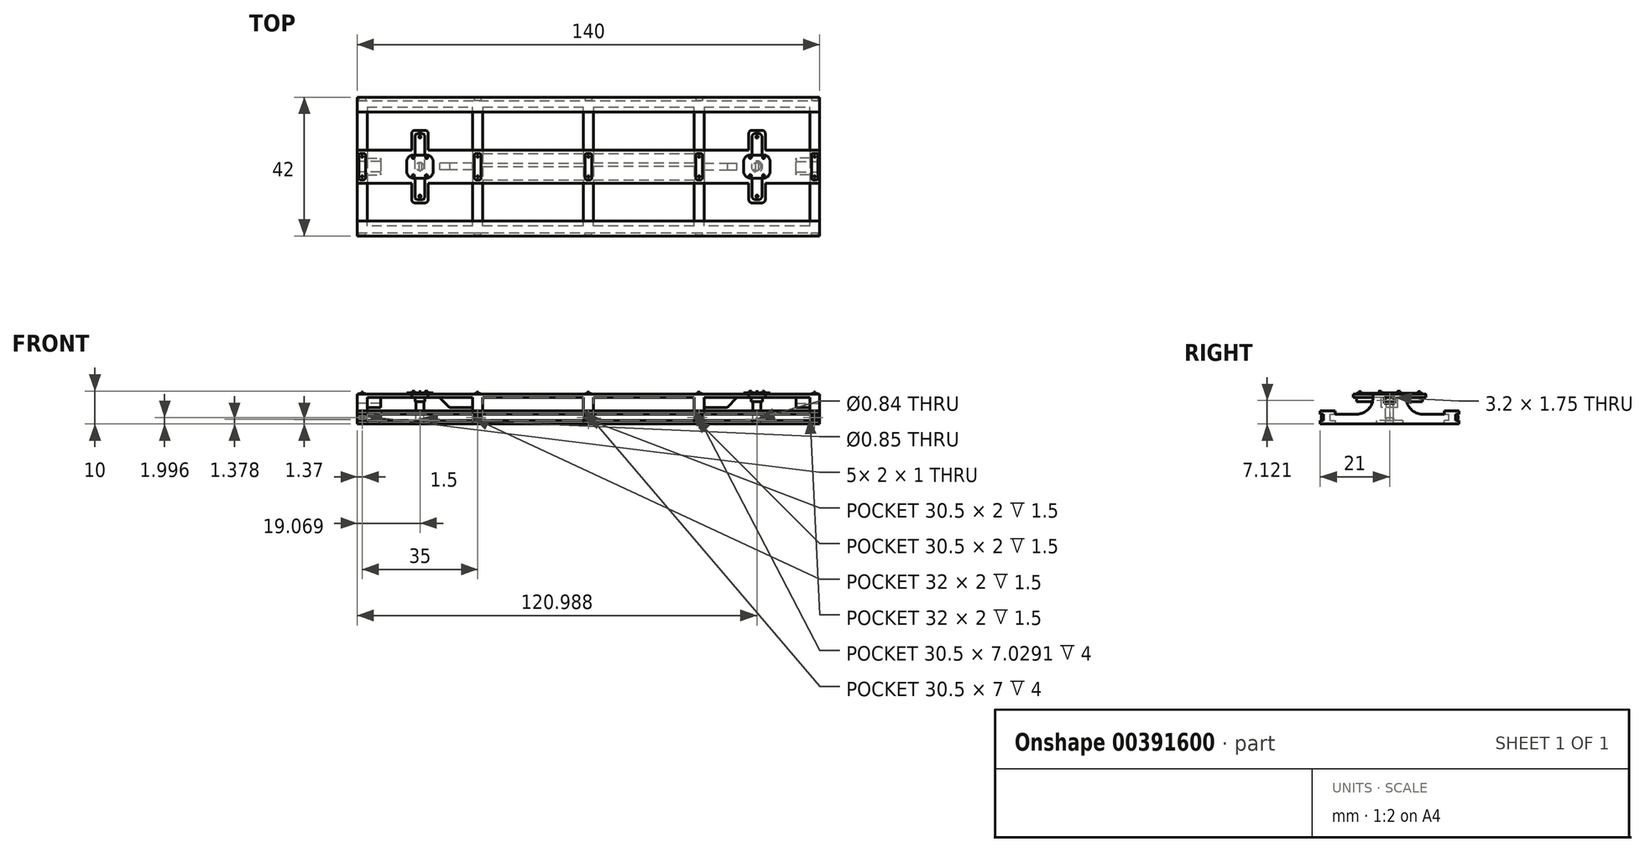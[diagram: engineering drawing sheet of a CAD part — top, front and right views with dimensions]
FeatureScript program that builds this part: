
annotation { "Feature Type Name" : "Feature", "Feature Type Description" : "" }
export const myFeature = defineFeature(function(context is Context, id is Id, definition is map)
    precondition{}
    {
        {
            var Q0;
            Q0=qCreatedBy(makeId("Right.planeOp"),FACE);
            var sketch = newSketch(context, id + "F0", { "sketchPlane" : qUnion([Q0])});
            skLineSegment(sketch, "E0", {"start": v(-20, 2.38) * mm, "end": v(-20, -0.62) * mm});
            skLineSegment(sketch, "E1", {"start": v(-20, -0.62) * mm, "end": v(20, -0.62) * mm});
            skLineSegment(sketch, "E2", {"start": v(20, -0.62) * mm, "end": v(20, 2.38) * mm});
            skLineSegment(sketch, "E3", {"start": v(20, 2.38) * mm, "end": v(10, 2.38) * mm});
            skLineSegment(sketch, "E4", {"start": v(5, 7.38) * mm, "end": v(5, 8.38) * mm});
            skLineSegment(sketch, "E5", {"start": v(5, 8.38) * mm, "end": v(-5, 8.38) * mm});
            skLineSegment(sketch, "E6", {"start": v(-5, 8.38) * mm, "end": v(-5, 7.38) * mm});
            skLineSegment(sketch, "E7", {"start": v(-10, 2.38) * mm, "end": v(-20, 2.38) * mm});
            skPoint(sketch, "E8.visualSharp", {"position": v(-5, 2.38) * mm});
            skArc(sketch, "E8.filletArc", {"start": v(-10, 2.38) * mm, "mid": v(-6.46, 3.84) * mm, "end": v(-5, 7.38) * mm});
            skPoint(sketch, "E9.visualSharp", {"position": v(5, 2.38) * mm});
            skArc(sketch, "E9.filletArc", {"start": v(5, 7.38) * mm, "mid": v(6.46, 3.84) * mm, "end": v(10, 2.38) * mm});
            skSolve(sketch);
        }
        {
            var Q0;
            Q0=makeQuery(id+"F0.imprint","IMPRINT",FACE,{"disambiguationData":[TD([[makeQuery(id+"F0.imprint","IMPRINT",EDGE,{"derivedFrom":sQuery(id+"F0.wireOp",EDGE,"E0")}),1.0]])]});
            extrude(context, id + "F1", {"entities" : qUnion([Q0]), "endBound" : BoundingType.SYMMETRIC, "depth" : 140 * mm});
        }
        {
            var Q0;
            Q0=makeQuery(id+"F1.opExtrude","SWEPT_FACE",FACE,{"disambiguationData":[OSD([sQuery(id+"F0.wireOp",EDGE,"E0")])]});
            var sketch = newSketch(context, id + "F2", { "sketchPlane" : qUnion([Q0])});
            skLineSegment(sketch, "E10.bottom", {"start": v(-67, 7.38) * mm, "end": v(-35, 7.38) * mm});
            skLineSegment(sketch, "E10.top", {"start": v(-67, -0.62) * mm, "end": v(-35, -0.62) * mm});
            skLineSegment(sketch, "E10.left", {"start": v(-67, 7.38) * mm, "end": v(-67, -0.62) * mm});
            skLineSegment(sketch, "E10.right", {"start": v(-35, 7.38) * mm, "end": v(-35, -0.62) * mm});
            skLineSegment(sketch, "E11.bottom", {"start": v(35, 7.38) * mm, "end": v(67, 7.38) * mm});
            skLineSegment(sketch, "E11.top", {"start": v(35, -0.62) * mm, "end": v(67, -0.62) * mm});
            skLineSegment(sketch, "E11.left", {"start": v(35, 7.38) * mm, "end": v(35, -0.62) * mm});
            skLineSegment(sketch, "E11.right", {"start": v(67, 7.38) * mm, "end": v(67, -0.62) * mm});
            skSolve(sketch);
        }
        {
            var Q0;
            Q0 = qSketchRegion(id + "F2", true);
            extrude(context, id + "F3", {"entities" : qUnion([Q0]), "operationType" : NewBodyOperationType.REMOVE, "endBound" : BoundingType.THROUGH_ALL, "oppositeDirection" : true, "depth" : 25 * mm});
        }
        {
            var Q0;
            Q0=makeQuery(id+"F3.boolean.opBoolean","SPLIT",FACE,{"disambiguationData":[TD([makeQuery(id+"F3.opExtrude","SWEPT_FACE",FACE,{"disambiguationData":[OSD([sQuery(id+"F2.wireOp",EDGE,"E10.right")])]})])],"derivedFrom":makeQuery(id+"F1.opExtrude","SWEPT_FACE",FACE,{"disambiguationData":[OSD([sQuery(id+"F0.wireOp",EDGE,"E0")])]})});
            var sketch = newSketch(context, id + "F4", { "sketchPlane" : qUnion([Q0])});
            skLineSegment(sketch, "E12.bottom", {"start": v(-32, 7.38) * mm, "end": v(-1.5, 7.38) * mm});
            skLineSegment(sketch, "E12.top", {"start": v(-32, -0.62) * mm, "end": v(-1.5, -0.62) * mm});
            skLineSegment(sketch, "E12.left", {"start": v(-32, 7.38) * mm, "end": v(-32, -0.62) * mm});
            skLineSegment(sketch, "E12.right", {"start": v(-1.5, 7.38) * mm, "end": v(-1.5, -0.62) * mm});
            skLineSegment(sketch, "E13.bottom", {"start": v(32, 7.4) * mm, "end": v(1.5, 7.4) * mm});
            skLineSegment(sketch, "E13.top", {"start": v(32, -0.62) * mm, "end": v(1.5, -0.62) * mm});
            skLineSegment(sketch, "E13.left", {"start": v(32, 7.4) * mm, "end": v(32, -0.62) * mm});
            skLineSegment(sketch, "E13.right", {"start": v(1.5, 7.4) * mm, "end": v(1.5, -0.62) * mm});
            skSolve(sketch);
        }
        {
            var Q0;
            Q0 = qSketchRegion(id + "F4", true);
            extrude(context, id + "F5", {"entities" : qUnion([Q0]), "operationType" : NewBodyOperationType.REMOVE, "endBound" : BoundingType.THROUGH_ALL, "oppositeDirection" : true, "depth" : 25 * mm});
        }
        {
            var Q0;
            Q0=makeQuery(id+"F1.opExtrude","CAP_FACE",FACE,{"disambiguationData":[OSD([sQuery(id+"F0.wireOp",EDGE,"E0"),sQuery(id+"F0.wireOp",EDGE,"E1"),sQuery(id+"F0.wireOp",EDGE,"E2"),sQuery(id+"F0.wireOp",EDGE,"E3"),sQuery(id+"F0.wireOp",EDGE,"E4"),sQuery(id+"F0.wireOp",EDGE,"E5"),sQuery(id+"F0.wireOp",EDGE,"E6"),sQuery(id+"F0.wireOp",EDGE,"E7"),sQuery(id+"F0.wireOp",EDGE,"E8.filletArc"),sQuery(id+"F0.wireOp",EDGE,"E9.filletArc")])],"isStart":false});
            var sketch = newSketch(context, id + "F6", { "sketchPlane" : qUnion([Q0])});
            skLineSegment(sketch, "E14.bottom", {"start": v(-20, 2.38) * mm, "end": v(-18, 2.38) * mm});
            skLineSegment(sketch, "E14.top", {"start": v(-20, -0.62) * mm, "end": v(-18, -0.62) * mm});
            skLineSegment(sketch, "E14.left", {"start": v(-20, 2.38) * mm, "end": v(-20, -0.62) * mm});
            skLineSegment(sketch, "E14.right", {"start": v(-18, 2.38) * mm, "end": v(-18, -0.62) * mm});
            skLineSegment(sketch, "E15.bottom", {"start": v(20, 2.38) * mm, "end": v(18, 2.38) * mm});
            skLineSegment(sketch, "E15.top", {"start": v(20, -0.62) * mm, "end": v(18, -0.62) * mm});
            skLineSegment(sketch, "E15.left", {"start": v(20, 2.38) * mm, "end": v(20, -0.62) * mm});
            skLineSegment(sketch, "E15.right", {"start": v(18, 2.38) * mm, "end": v(18, -0.62) * mm});
            skSolve(sketch);
        }
        {
            var Q0;
            Q0 = qSketchRegion(id + "F6", true);
            extrude(context, id + "F7", {"entities" : qUnion([Q0]), "operationType" : NewBodyOperationType.ADD, "oppositeDirection" : true, "depth" : 140 * mm});
        }
        {
            var Q0;
            Q0=makeQuery(id+"F1.opExtrude","CAP_FACE",FACE,{"disambiguationData":[OSD([sQuery(id+"F0.wireOp",EDGE,"E0"),sQuery(id+"F0.wireOp",EDGE,"E1"),sQuery(id+"F0.wireOp",EDGE,"E2"),sQuery(id+"F0.wireOp",EDGE,"E3"),sQuery(id+"F0.wireOp",EDGE,"E4"),sQuery(id+"F0.wireOp",EDGE,"E5"),sQuery(id+"F0.wireOp",EDGE,"E6"),sQuery(id+"F0.wireOp",EDGE,"E7"),sQuery(id+"F0.wireOp",EDGE,"E8.filletArc"),sQuery(id+"F0.wireOp",EDGE,"E9.filletArc")])],"isStart":false});
            var sketch = newSketch(context, id + "F8", { "sketchPlane" : qUnion([Q0])});
            skLineSegment(sketch, "E16.bottom", {"start": v(-21, 3.38) * mm, "end": v(-16.5, 3.38) * mm});
            skLineSegment(sketch, "E16.top", {"start": v(-21, 2.38) * mm, "end": v(-16.5, 2.38) * mm});
            skLineSegment(sketch, "E16.left", {"start": v(-21, 3.38) * mm, "end": v(-21, 2.38) * mm});
            skLineSegment(sketch, "E16.right", {"start": v(-16.5, 3.38) * mm, "end": v(-16.5, 2.38) * mm});
            skLineSegment(sketch, "E17.bottom", {"start": v(16.5, 2.38) * mm, "end": v(21, 2.38) * mm});
            skLineSegment(sketch, "E17.top", {"start": v(16.5, 3.38) * mm, "end": v(21, 3.38) * mm});
            skLineSegment(sketch, "E17.left", {"start": v(16.5, 2.38) * mm, "end": v(16.5, 3.38) * mm});
            skLineSegment(sketch, "E17.right", {"start": v(21, 2.38) * mm, "end": v(21, 3.38) * mm});
            skSolve(sketch);
        }
        {
            var Q0;
            Q0 = qSketchRegion(id + "F8", true);
            extrude(context, id + "F9", {"entities" : qUnion([Q0]), "operationType" : NewBodyOperationType.ADD, "oppositeDirection" : true, "depth" : 140 * mm});
        }
        {
            var Q0;
            Q0=makeQuery(id+"F9.boolean.opBoolean","MERGE",FACE,{"derivedFrom":[makeQuery(id+"F1.opExtrude","CAP_FACE",FACE,{"disambiguationData":[OSD([sQuery(id+"F0.wireOp",EDGE,"E0"),sQuery(id+"F0.wireOp",EDGE,"E1"),sQuery(id+"F0.wireOp",EDGE,"E2"),sQuery(id+"F0.wireOp",EDGE,"E3"),sQuery(id+"F0.wireOp",EDGE,"E4"),sQuery(id+"F0.wireOp",EDGE,"E5"),sQuery(id+"F0.wireOp",EDGE,"E6"),sQuery(id+"F0.wireOp",EDGE,"E7"),sQuery(id+"F0.wireOp",EDGE,"E8.filletArc"),sQuery(id+"F0.wireOp",EDGE,"E9.filletArc")])],"isStart":false}),makeQuery(id+"F9.opExtrude","CAP_FACE",FACE,{"disambiguationData":[OSD([sQuery(id+"F8.wireOp",EDGE,"E16.bottom"),sQuery(id+"F8.wireOp",EDGE,"E16.top"),sQuery(id+"F8.wireOp",EDGE,"E16.left"),sQuery(id+"F8.wireOp",EDGE,"E16.right")])],"isStart":true}),makeQuery(id+"F9.opExtrude","CAP_FACE",FACE,{"disambiguationData":[OSD([sQuery(id+"F8.wireOp",EDGE,"E17.bottom"),sQuery(id+"F8.wireOp",EDGE,"E17.top"),sQuery(id+"F8.wireOp",EDGE,"E17.left"),sQuery(id+"F8.wireOp",EDGE,"E17.right")])],"isStart":true})]});
            var sketch = newSketch(context, id + "F10", { "sketchPlane" : qUnion([Q0])});
            skLineSegment(sketch, "E18.bottom", {"start": v(-16.5, -0.62) * mm, "end": v(-21, -0.62) * mm});
            skLineSegment(sketch, "E18.top", {"start": v(-16.5, 0.38) * mm, "end": v(-21, 0.38) * mm});
            skLineSegment(sketch, "E18.left", {"start": v(-16.5, -0.62) * mm, "end": v(-16.5, 0.38) * mm});
            skLineSegment(sketch, "E18.right", {"start": v(-21, -0.62) * mm, "end": v(-21, 0.38) * mm});
            skLineSegment(sketch, "E19.bottom", {"start": v(16.5, 0.38) * mm, "end": v(21, 0.38) * mm});
            skLineSegment(sketch, "E19.top", {"start": v(16.5, -0.62) * mm, "end": v(21, -0.62) * mm});
            skLineSegment(sketch, "E19.left", {"start": v(16.5, 0.38) * mm, "end": v(16.5, -0.62) * mm});
            skLineSegment(sketch, "E19.right", {"start": v(21, 0.38) * mm, "end": v(21, -0.62) * mm});
            skSolve(sketch);
        }
        {
            var Q0;
            Q0 = qSketchRegion(id + "F10", true);
            extrude(context, id + "F11", {"entities" : qUnion([Q0]), "operationType" : NewBodyOperationType.ADD, "oppositeDirection" : true, "depth" : 140 * mm});
        }
        {
            var Q0;
            Q0=makeQuery(id+"F3.boolean.opBoolean","COPY",FACE,{"derivedFrom":makeQuery(id+"F3.opExtrude","SWEPT_FACE",FACE,{"disambiguationData":[OSD([sQuery(id+"F2.wireOp",EDGE,"E11.bottom")])]})});
            var sketch = newSketch(context, id + "F12", { "sketchPlane" : qUnion([Q0])});
            skCircle(sketch, "E20", {"center": v(51, 0) * mm, "radius": 1.2 * mm});
            skCircle(sketch, "E21", {"center": v(-51, 0) * mm, "radius": 1.2 * mm});
            skSolve(sketch);
        }
        {
            var Q0;
            Q0 = qSketchRegion(id + "F12", true);
            extrude(context, id + "F13", {"entities" : qUnion([Q0]), "operationType" : NewBodyOperationType.ADD, "depth" : 8 * mm});
        }
        {
            var Q0;
            Q0=makeQuery(id+"F3.boolean.opBoolean","COPY",FACE,{"derivedFrom":makeQuery(id+"F3.opExtrude","SWEPT_FACE",FACE,{"disambiguationData":[OSD([sQuery(id+"F2.wireOp",EDGE,"E10.bottom")])]})});
            var sketch = newSketch(context, id + "F14", { "sketchPlane" : qUnion([Q0])});
            skLineSegment(sketch, "E22.bottom", {"start": v(-52.5, 10) * mm, "end": v(-49.5, 10) * mm});
            skLineSegment(sketch, "E22.top", {"start": v(-52.5, -10) * mm, "end": v(-49.5, -10) * mm});
            skLineSegment(sketch, "E22.left", {"start": v(-52.5, 10) * mm, "end": v(-52.5, -10) * mm});
            skLineSegment(sketch, "E22.right", {"start": v(-49.5, 10) * mm, "end": v(-49.5, -10) * mm});
            skCircle(sketch, "E23", {"center": v(51.03, 0) * mm, "radius": 1.7 * mm});
            skSolve(sketch);
        }
        {
            var Q0;
            Q0 = qSketchRegion(id + "F14", true);
            extrude(context, id + "F15", {"entities" : qUnion([Q0]), "operationType" : NewBodyOperationType.ADD, "depth" : 1.2 * mm});
        }
        {
            var Q0;
            Q0=makeQuery(id+"F1.opExtrude","SWEPT_FACE",FACE,{"disambiguationData":[OSD([sQuery(id+"F0.wireOp",EDGE,"E5")])]});
            var sketch = newSketch(context, id + "F16", { "sketchPlane" : qUnion([Q0])});
            skLineSegment(sketch, "E24.bottom", {"start": v(-53, 3.5) * mm, "end": v(-49, 3.5) * mm});
            skLineSegment(sketch, "E24.top", {"start": v(-53, -3.5) * mm, "end": v(-49, -3.5) * mm});
            skLineSegment(sketch, "E24.left", {"start": v(-55, 1.5) * mm, "end": v(-55, -1.5) * mm});
            skLineSegment(sketch, "E24.right", {"start": v(-47, 1.5) * mm, "end": v(-47, -1.5) * mm});
            skLineSegment(sketch, "E25.bottom", {"start": v(49, 3.5) * mm, "end": v(53, 3.5) * mm});
            skLineSegment(sketch, "E25.top", {"start": v(49, -3.5) * mm, "end": v(53, -3.5) * mm});
            skLineSegment(sketch, "E25.left", {"start": v(47, 1.5) * mm, "end": v(47, -1.5) * mm});
            skLineSegment(sketch, "E25.right", {"start": v(55, 1.5) * mm, "end": v(55, -1.5) * mm});
            skPoint(sketch, "E26.visualSharp", {"position": v(47, 3.5) * mm});
            skArc(sketch, "E26.filletArc", {"start": v(49, 3.5) * mm, "mid": v(47.59, 2.91) * mm, "end": v(47, 1.5) * mm});
            skPoint(sketch, "E27.visualSharp", {"position": v(55, -3.5) * mm});
            skArc(sketch, "E27.filletArc", {"start": v(53, -3.5) * mm, "mid": v(54.41, -2.91) * mm, "end": v(55, -1.5) * mm});
            skPoint(sketch, "E28.visualSharp", {"position": v(55, 3.5) * mm});
            skArc(sketch, "E28.filletArc", {"start": v(55, 1.5) * mm, "mid": v(54.41, 2.91) * mm, "end": v(53, 3.5) * mm});
            skPoint(sketch, "E29.visualSharp", {"position": v(47, -3.5) * mm});
            skArc(sketch, "E29.filletArc", {"start": v(47, -1.5) * mm, "mid": v(47.59, -2.91) * mm, "end": v(49, -3.5) * mm});
            skPoint(sketch, "E30.visualSharp", {"position": v(-47, 3.5) * mm});
            skArc(sketch, "E30.filletArc", {"start": v(-47, 1.5) * mm, "mid": v(-47.59, 2.91) * mm, "end": v(-49, 3.5) * mm});
            skPoint(sketch, "E31.visualSharp", {"position": v(-55, 3.5) * mm});
            skArc(sketch, "E31.filletArc", {"start": v(-53, 3.5) * mm, "mid": v(-54.41, 2.91) * mm, "end": v(-55, 1.5) * mm});
            skPoint(sketch, "E32.visualSharp", {"position": v(-55, -3.5) * mm});
            skArc(sketch, "E32.filletArc", {"start": v(-55, -1.5) * mm, "mid": v(-54.41, -2.91) * mm, "end": v(-53, -3.5) * mm});
            skPoint(sketch, "E33.visualSharp", {"position": v(-47, -3.5) * mm});
            skArc(sketch, "E33.filletArc", {"start": v(-49, -3.5) * mm, "mid": v(-47.59, -2.91) * mm, "end": v(-47, -1.5) * mm});
            skSolve(sketch);
        }
        {
            var Q0;
            Q0 = qSketchRegion(id + "F16", true);
            extrude(context, id + "F17", {"entities" : qUnion([Q0]), "operationType" : NewBodyOperationType.ADD, "depth" : 0.5 * mm});
        }
        {
            var Q0;
            Q0=makeQuery(id+"F11.boolean.opBoolean","MERGE",FACE,{"derivedFrom":[makeQuery(id+"F9.boolean.opBoolean","MERGE",FACE,{"derivedFrom":[makeQuery(id+"F1.opExtrude","CAP_FACE",FACE,{"disambiguationData":[OSD([sQuery(id+"F0.wireOp",EDGE,"E0"),sQuery(id+"F0.wireOp",EDGE,"E1"),sQuery(id+"F0.wireOp",EDGE,"E2"),sQuery(id+"F0.wireOp",EDGE,"E3"),sQuery(id+"F0.wireOp",EDGE,"E4"),sQuery(id+"F0.wireOp",EDGE,"E5"),sQuery(id+"F0.wireOp",EDGE,"E6"),sQuery(id+"F0.wireOp",EDGE,"E7"),sQuery(id+"F0.wireOp",EDGE,"E8.filletArc"),sQuery(id+"F0.wireOp",EDGE,"E9.filletArc")])],"isStart":false}),makeQuery(id+"F9.opExtrude","CAP_FACE",FACE,{"disambiguationData":[OSD([sQuery(id+"F8.wireOp",EDGE,"E16.bottom"),sQuery(id+"F8.wireOp",EDGE,"E16.top"),sQuery(id+"F8.wireOp",EDGE,"E16.left"),sQuery(id+"F8.wireOp",EDGE,"E16.right")])],"isStart":true}),makeQuery(id+"F9.opExtrude","CAP_FACE",FACE,{"disambiguationData":[OSD([sQuery(id+"F8.wireOp",EDGE,"E17.bottom"),sQuery(id+"F8.wireOp",EDGE,"E17.top"),sQuery(id+"F8.wireOp",EDGE,"E17.left"),sQuery(id+"F8.wireOp",EDGE,"E17.right")])],"isStart":true})]}),makeQuery(id+"F11.opExtrude","CAP_FACE",FACE,{"disambiguationData":[OSD([sQuery(id+"F10.wireOp",EDGE,"E18.bottom"),sQuery(id+"F10.wireOp",EDGE,"E18.top"),sQuery(id+"F10.wireOp",EDGE,"E18.left"),sQuery(id+"F10.wireOp",EDGE,"E18.right")])],"isStart":true}),makeQuery(id+"F11.opExtrude","CAP_FACE",FACE,{"disambiguationData":[OSD([sQuery(id+"F10.wireOp",EDGE,"E19.bottom"),sQuery(id+"F10.wireOp",EDGE,"E19.top"),sQuery(id+"F10.wireOp",EDGE,"E19.left"),sQuery(id+"F10.wireOp",EDGE,"E19.right")])],"isStart":true})]});
            var sketch = newSketch(context, id + "F18", { "sketchPlane" : qUnion([Q0])});
            skLineSegment(sketch, "E34.bottom", {"start": v(-2.5, 8.38) * mm, "end": v(2.5, 8.38) * mm});
            skLineSegment(sketch, "E34.top", {"start": v(-2.5, 4.38) * mm, "end": v(2.5, 4.38) * mm});
            skLineSegment(sketch, "E34.left", {"start": v(-2.5, 8.38) * mm, "end": v(-2.5, 4.38) * mm});
            skLineSegment(sketch, "E34.right", {"start": v(2.5, 8.38) * mm, "end": v(2.5, 4.38) * mm});
            skSolve(sketch);
        }
        {
            var Q0;
            Q0=makeQuery(id+"F18.imprint","IMPRINT",FACE,{"disambiguationData":[TD([[makeQuery(id+"F18.imprint","IMPRINT",EDGE,{"derivedFrom":sQuery(id+"F18.wireOp",EDGE,"E34.bottom")}),1.0]])]});
            extrude(context, id + "F19", {"entities" : qUnion([Q0]), "operationType" : NewBodyOperationType.ADD, "oppositeDirection" : true, "depth" : 7.1 * mm});
        }
        {
            var Q0;
            Q0=makeQuery(id+"F11.boolean.opBoolean","MERGE",FACE,{"derivedFrom":[makeQuery(id+"F9.boolean.opBoolean","MERGE",FACE,{"derivedFrom":[makeQuery(id+"F1.opExtrude","CAP_FACE",FACE,{"disambiguationData":[OSD([sQuery(id+"F0.wireOp",EDGE,"E0"),sQuery(id+"F0.wireOp",EDGE,"E1"),sQuery(id+"F0.wireOp",EDGE,"E2"),sQuery(id+"F0.wireOp",EDGE,"E3"),sQuery(id+"F0.wireOp",EDGE,"E4"),sQuery(id+"F0.wireOp",EDGE,"E5"),sQuery(id+"F0.wireOp",EDGE,"E6"),sQuery(id+"F0.wireOp",EDGE,"E7"),sQuery(id+"F0.wireOp",EDGE,"E8.filletArc"),sQuery(id+"F0.wireOp",EDGE,"E9.filletArc")])],"isStart":false}),makeQuery(id+"F9.opExtrude","CAP_FACE",FACE,{"disambiguationData":[OSD([sQuery(id+"F8.wireOp",EDGE,"E16.bottom"),sQuery(id+"F8.wireOp",EDGE,"E16.top"),sQuery(id+"F8.wireOp",EDGE,"E16.left"),sQuery(id+"F8.wireOp",EDGE,"E16.right")])],"isStart":true}),makeQuery(id+"F9.opExtrude","CAP_FACE",FACE,{"disambiguationData":[OSD([sQuery(id+"F8.wireOp",EDGE,"E17.bottom"),sQuery(id+"F8.wireOp",EDGE,"E17.top"),sQuery(id+"F8.wireOp",EDGE,"E17.left"),sQuery(id+"F8.wireOp",EDGE,"E17.right")])],"isStart":true})]}),makeQuery(id+"F11.opExtrude","CAP_FACE",FACE,{"disambiguationData":[OSD([sQuery(id+"F10.wireOp",EDGE,"E18.bottom"),sQuery(id+"F10.wireOp",EDGE,"E18.top"),sQuery(id+"F10.wireOp",EDGE,"E18.left"),sQuery(id+"F10.wireOp",EDGE,"E18.right")])],"isStart":true}),makeQuery(id+"F11.opExtrude","CAP_FACE",FACE,{"disambiguationData":[OSD([sQuery(id+"F10.wireOp",EDGE,"E19.bottom"),sQuery(id+"F10.wireOp",EDGE,"E19.top"),sQuery(id+"F10.wireOp",EDGE,"E19.left"),sQuery(id+"F10.wireOp",EDGE,"E19.right")])],"isStart":true})]});
            var sketch = newSketch(context, id + "F20", { "sketchPlane" : qUnion([Q0])});
            skLineSegment(sketch, "E35.bottom", {"start": v(-1.6, 7.38) * mm, "end": v(1.6, 7.38) * mm});
            skLineSegment(sketch, "E35.top", {"start": v(-1.6, 5.63) * mm, "end": v(1.6, 5.63) * mm});
            skLineSegment(sketch, "E35.left", {"start": v(-1.6, 7.38) * mm, "end": v(-1.6, 5.63) * mm});
            skLineSegment(sketch, "E35.right", {"start": v(1.6, 7.38) * mm, "end": v(1.6, 5.63) * mm});
            skSolve(sketch);
        }
        {
            var Q0;
            Q0=makeQuery(id+"F20.imprint","IMPRINT",FACE,{"disambiguationData":[TD([[makeQuery(id+"F20.imprint","IMPRINT",EDGE,{"derivedFrom":sQuery(id+"F20.wireOp",EDGE,"E35.bottom")}),-1.0]])]});
            extrude(context, id + "F21", {"entities" : qUnion([Q0]), "operationType" : NewBodyOperationType.REMOVE, "oppositeDirection" : true, "depth" : 10 * mm});
        }
        {
            var Q0;
            Q0=makeQuery(id+"F11.boolean.opBoolean","MERGE",FACE,{"derivedFrom":[makeQuery(id+"F9.boolean.opBoolean","MERGE",FACE,{"derivedFrom":[makeQuery(id+"F1.opExtrude","CAP_FACE",FACE,{"disambiguationData":[OSD([sQuery(id+"F0.wireOp",EDGE,"E0"),sQuery(id+"F0.wireOp",EDGE,"E1"),sQuery(id+"F0.wireOp",EDGE,"E2"),sQuery(id+"F0.wireOp",EDGE,"E3"),sQuery(id+"F0.wireOp",EDGE,"E4"),sQuery(id+"F0.wireOp",EDGE,"E5"),sQuery(id+"F0.wireOp",EDGE,"E6"),sQuery(id+"F0.wireOp",EDGE,"E7"),sQuery(id+"F0.wireOp",EDGE,"E8.filletArc"),sQuery(id+"F0.wireOp",EDGE,"E9.filletArc")])],"isStart":true}),makeQuery(id+"F9.opExtrude","CAP_FACE",FACE,{"disambiguationData":[OSD([sQuery(id+"F8.wireOp",EDGE,"E16.bottom"),sQuery(id+"F8.wireOp",EDGE,"E16.top"),sQuery(id+"F8.wireOp",EDGE,"E16.left"),sQuery(id+"F8.wireOp",EDGE,"E16.right")])],"isStart":false}),makeQuery(id+"F9.opExtrude","CAP_FACE",FACE,{"disambiguationData":[OSD([sQuery(id+"F8.wireOp",EDGE,"E17.bottom"),sQuery(id+"F8.wireOp",EDGE,"E17.top"),sQuery(id+"F8.wireOp",EDGE,"E17.left"),sQuery(id+"F8.wireOp",EDGE,"E17.right")])],"isStart":false})]}),makeQuery(id+"F11.opExtrude","CAP_FACE",FACE,{"disambiguationData":[OSD([sQuery(id+"F10.wireOp",EDGE,"E18.bottom"),sQuery(id+"F10.wireOp",EDGE,"E18.top"),sQuery(id+"F10.wireOp",EDGE,"E18.left"),sQuery(id+"F10.wireOp",EDGE,"E18.right")])],"isStart":false}),makeQuery(id+"F11.opExtrude","CAP_FACE",FACE,{"disambiguationData":[OSD([sQuery(id+"F10.wireOp",EDGE,"E19.bottom"),sQuery(id+"F10.wireOp",EDGE,"E19.top"),sQuery(id+"F10.wireOp",EDGE,"E19.left"),sQuery(id+"F10.wireOp",EDGE,"E19.right")])],"isStart":false})]});
            var sketch = newSketch(context, id + "F22", { "sketchPlane" : qUnion([Q0])});
            skLineSegment(sketch, "E36.bottom", {"start": v(-2.5, 8.38) * mm, "end": v(2.5, 8.38) * mm});
            skLineSegment(sketch, "E36.top", {"start": v(-2.5, 4.38) * mm, "end": v(2.5, 4.38) * mm});
            skLineSegment(sketch, "E36.left", {"start": v(-2.5, 8.38) * mm, "end": v(-2.5, 4.38) * mm});
            skLineSegment(sketch, "E36.right", {"start": v(2.5, 8.38) * mm, "end": v(2.5, 4.38) * mm});
            skSolve(sketch);
        }
        {
            var Q0;
            Q0=makeQuery(id+"F22.imprint","IMPRINT",FACE,{"disambiguationData":[TD([[makeQuery(id+"F22.imprint","IMPRINT",EDGE,{"derivedFrom":sQuery(id+"F22.wireOp",EDGE,"E36.bottom")}),-1.0]])]});
            extrude(context, id + "F23", {"entities" : qUnion([Q0]), "operationType" : NewBodyOperationType.ADD, "oppositeDirection" : true, "depth" : 7.1 * mm});
        }
        {
            var Q0;
            Q0=makeQuery(id+"F11.boolean.opBoolean","MERGE",FACE,{"derivedFrom":[makeQuery(id+"F9.boolean.opBoolean","MERGE",FACE,{"derivedFrom":[makeQuery(id+"F1.opExtrude","CAP_FACE",FACE,{"disambiguationData":[OSD([sQuery(id+"F0.wireOp",EDGE,"E0"),sQuery(id+"F0.wireOp",EDGE,"E1"),sQuery(id+"F0.wireOp",EDGE,"E2"),sQuery(id+"F0.wireOp",EDGE,"E3"),sQuery(id+"F0.wireOp",EDGE,"E4"),sQuery(id+"F0.wireOp",EDGE,"E5"),sQuery(id+"F0.wireOp",EDGE,"E6"),sQuery(id+"F0.wireOp",EDGE,"E7"),sQuery(id+"F0.wireOp",EDGE,"E8.filletArc"),sQuery(id+"F0.wireOp",EDGE,"E9.filletArc")])],"isStart":true}),makeQuery(id+"F9.opExtrude","CAP_FACE",FACE,{"disambiguationData":[OSD([sQuery(id+"F8.wireOp",EDGE,"E16.bottom"),sQuery(id+"F8.wireOp",EDGE,"E16.top"),sQuery(id+"F8.wireOp",EDGE,"E16.left"),sQuery(id+"F8.wireOp",EDGE,"E16.right")])],"isStart":false}),makeQuery(id+"F9.opExtrude","CAP_FACE",FACE,{"disambiguationData":[OSD([sQuery(id+"F8.wireOp",EDGE,"E17.bottom"),sQuery(id+"F8.wireOp",EDGE,"E17.top"),sQuery(id+"F8.wireOp",EDGE,"E17.left"),sQuery(id+"F8.wireOp",EDGE,"E17.right")])],"isStart":false})]}),makeQuery(id+"F11.opExtrude","CAP_FACE",FACE,{"disambiguationData":[OSD([sQuery(id+"F10.wireOp",EDGE,"E18.bottom"),sQuery(id+"F10.wireOp",EDGE,"E18.top"),sQuery(id+"F10.wireOp",EDGE,"E18.left"),sQuery(id+"F10.wireOp",EDGE,"E18.right")])],"isStart":false}),makeQuery(id+"F11.opExtrude","CAP_FACE",FACE,{"disambiguationData":[OSD([sQuery(id+"F10.wireOp",EDGE,"E19.bottom"),sQuery(id+"F10.wireOp",EDGE,"E19.top"),sQuery(id+"F10.wireOp",EDGE,"E19.left"),sQuery(id+"F10.wireOp",EDGE,"E19.right")])],"isStart":false})]});
            var sketch = newSketch(context, id + "F24", { "sketchPlane" : qUnion([Q0])});
            skLineSegment(sketch, "E37.bottom", {"start": v(-1.6, 7.38) * mm, "end": v(1.6, 7.38) * mm});
            skLineSegment(sketch, "E37.top", {"start": v(-1.6, 5.63) * mm, "end": v(1.6, 5.63) * mm});
            skLineSegment(sketch, "E37.left", {"start": v(-1.6, 7.38) * mm, "end": v(-1.6, 5.63) * mm});
            skLineSegment(sketch, "E37.right", {"start": v(1.6, 7.38) * mm, "end": v(1.6, 5.63) * mm});
            skSolve(sketch);
        }
        {
            var Q0;
            Q0=makeQuery(id+"F24.imprint","IMPRINT",FACE,{"disambiguationData":[TD([[makeQuery(id+"F24.imprint","IMPRINT",EDGE,{"derivedFrom":sQuery(id+"F24.wireOp",EDGE,"E37.bottom")}),-1.0]])]});
            extrude(context, id + "F25", {"entities" : qUnion([Q0]), "operationType" : NewBodyOperationType.REMOVE, "oppositeDirection" : true, "depth" : 10 * mm});
        }
        {
            var Q0;
            {var subQ4=makeQuery(id+"F3.opExtrude","SWEPT_FACE",FACE,{"disambiguationData":[OSD([sQuery(id+"F2.wireOp",EDGE,"E10.right")])]});var subQ5=makeQuery(id+"F3.opExtrude","SWEPT_FACE",FACE,{"disambiguationData":[OSD([sQuery(id+"F2.wireOp",EDGE,"E11.left")])]});var subQ6=sQuery(id+"F0.wireOp",EDGE,"E1");var subQ7=makeQuery(id+"F1.opExtrude","SWEPT_FACE",FACE,{"disambiguationData":[OSD([subQ6])]});var subQ8=makeQuery(id+"F3.boolean.opBoolean","SPLIT",FACE,{"disambiguationData":[TD([subQ4])],"derivedFrom":subQ7});Q0=makeQuery(id+"F11.boolean.opBoolean","MERGE",FACE,{"derivedFrom":[makeQuery(id+"F7.boolean.opBoolean","MERGE",FACE,{"derivedFrom":[makeQuery(id+"F3.boolean.opBoolean","SPLIT",FACE,{"disambiguationData":[TD([makeQuery(id+"F3.opExtrude","SWEPT_FACE",FACE,{"disambiguationData":[OSD([sQuery(id+"F2.wireOp",EDGE,"E10.left")])]})])],"derivedFrom":subQ7}),makeQuery(id+"F3.boolean.opBoolean","SPLIT",FACE,{"disambiguationData":[TD([makeQuery(id+"F3.opExtrude","SWEPT_FACE",FACE,{"disambiguationData":[OSD([sQuery(id+"F2.wireOp",EDGE,"E11.right")])]})])],"derivedFrom":subQ7}),makeQuery(id+"F5.boolean.opBoolean","SPLIT",FACE,{"disambiguationData":[TD([makeQuery(id+"F3.boolean.opBoolean","COPY",FACE,{"derivedFrom":subQ4})])],"derivedFrom":subQ8}),makeQuery(id+"F5.boolean.opBoolean","SPLIT",FACE,{"disambiguationData":[TD([makeQuery(id+"F3.boolean.opBoolean","COPY",FACE,{"derivedFrom":subQ5})])],"derivedFrom":subQ8}),makeQuery(id+"F5.boolean.opBoolean","SPLIT",FACE,{"disambiguationData":[TD([makeQuery(id+"F5.opExtrude","SWEPT_FACE",FACE,{"disambiguationData":[OSD([sQuery(id+"F4.wireOp",EDGE,"E12.right")])]})])],"derivedFrom":subQ8}),makeQuery(id+"F7.opExtrude","SWEPT_FACE",FACE,{"disambiguationData":[OSD([sQuery(id+"F6.wireOp",EDGE,"E14.top")])]}),makeQuery(id+"F7.opExtrude","SWEPT_FACE",FACE,{"disambiguationData":[OSD([sQuery(id+"F6.wireOp",EDGE,"E15.top")])]})]}),makeQuery(id+"F11.opExtrude","SWEPT_FACE",FACE,{"disambiguationData":[OSD([sQuery(id+"F10.wireOp",EDGE,"E18.bottom")])]}),makeQuery(id+"F11.opExtrude","SWEPT_FACE",FACE,{"disambiguationData":[OSD([sQuery(id+"F10.wireOp",EDGE,"E19.top")])]})]});}
            var sketch = newSketch(context, id + "F26", { "sketchPlane" : qUnion([Q0])});
            skLineSegment(sketch, "E38.bottom", {"start": v(-35, -4) * mm, "end": v(35, -4) * mm});
            skLineSegment(sketch, "E38.top", {"start": v(-35, 4) * mm, "end": v(35, 4) * mm});
            skLineSegment(sketch, "E38.left", {"start": v(-35, -4) * mm, "end": v(-35, 4) * mm});
            skLineSegment(sketch, "E38.right", {"start": v(35, -4) * mm, "end": v(35, 4) * mm});
            skSolve(sketch);
        }
        {
            var Q0;
            Q0 = qSketchRegion(id + "F26", true);
            extrude(context, id + "F27", {"entities" : qUnion([Q0]), "operationType" : NewBodyOperationType.ADD, "oppositeDirection" : true, "depth" : 1 * mm});
        }
        {
            var Q0;
            {var subQ4=makeQuery(id+"F3.opExtrude","SWEPT_FACE",FACE,{"disambiguationData":[OSD([sQuery(id+"F2.wireOp",EDGE,"E10.right")])]});var subQ5=makeQuery(id+"F3.opExtrude","SWEPT_FACE",FACE,{"disambiguationData":[OSD([sQuery(id+"F2.wireOp",EDGE,"E11.left")])]});var subQ6=sQuery(id+"F0.wireOp",EDGE,"E2");var subQ7=makeQuery(id+"F1.opExtrude","SWEPT_FACE",FACE,{"disambiguationData":[OSD([subQ6])]});var subQ8=makeQuery(id+"F3.boolean.opBoolean","SPLIT",FACE,{"disambiguationData":[TD([subQ4])],"derivedFrom":subQ7});Q0=makeQuery(id+"F7.boolean.opBoolean","MERGE",FACE,{"derivedFrom":[makeQuery(id+"F3.boolean.opBoolean","SPLIT",FACE,{"disambiguationData":[TD([makeQuery(id+"F3.opExtrude","SWEPT_FACE",FACE,{"disambiguationData":[OSD([sQuery(id+"F2.wireOp",EDGE,"E10.left")])]})])],"derivedFrom":subQ7}),makeQuery(id+"F3.boolean.opBoolean","SPLIT",FACE,{"disambiguationData":[TD([makeQuery(id+"F3.opExtrude","SWEPT_FACE",FACE,{"disambiguationData":[OSD([sQuery(id+"F2.wireOp",EDGE,"E11.right")])]})])],"derivedFrom":subQ7}),makeQuery(id+"F5.boolean.opBoolean","SPLIT",FACE,{"disambiguationData":[TD([makeQuery(id+"F3.boolean.opBoolean","COPY",FACE,{"derivedFrom":subQ4})])],"derivedFrom":subQ8}),makeQuery(id+"F5.boolean.opBoolean","SPLIT",FACE,{"disambiguationData":[TD([makeQuery(id+"F3.boolean.opBoolean","COPY",FACE,{"derivedFrom":subQ5})])],"derivedFrom":subQ8}),makeQuery(id+"F5.boolean.opBoolean","SPLIT",FACE,{"disambiguationData":[TD([makeQuery(id+"F5.opExtrude","SWEPT_FACE",FACE,{"disambiguationData":[OSD([sQuery(id+"F4.wireOp",EDGE,"E12.right")])]})])],"derivedFrom":subQ8}),makeQuery(id+"F7.opExtrude","SWEPT_FACE",FACE,{"disambiguationData":[OSD([sQuery(id+"F6.wireOp",EDGE,"E15.left")])]})]});}
            var sketch = newSketch(context, id + "F28", { "sketchPlane" : qUnion([Q0])});
            skLineSegment(sketch, "E39.bottom", {"start": v(-69.5, 1.88) * mm, "end": v(-67.5, 1.88) * mm});
            skLineSegment(sketch, "E39.top", {"start": v(-69.5, 0.88) * mm, "end": v(-67.5, 0.88) * mm});
            skLineSegment(sketch, "E39.left", {"start": v(-69.5, 1.88) * mm, "end": v(-69.5, 0.88) * mm});
            skLineSegment(sketch, "E39.right", {"start": v(-67.5, 1.88) * mm, "end": v(-67.5, 0.88) * mm});
            skLineSegment(sketch, "E40.bottom", {"start": v(-34.5, 1.88) * mm, "end": v(-32.5, 1.88) * mm});
            skLineSegment(sketch, "E40.top", {"start": v(-34.5, 0.88) * mm, "end": v(-32.5, 0.88) * mm});
            skLineSegment(sketch, "E40.left", {"start": v(-34.5, 1.88) * mm, "end": v(-34.5, 0.88) * mm});
            skLineSegment(sketch, "E40.right", {"start": v(-32.5, 1.88) * mm, "end": v(-32.5, 0.88) * mm});
            skPoint(sketch, "E41.oppositeSnap0", {"position": v(-33.5, 0.88) * mm});
            skLineSegment(sketch, "E41.bottom", {"start": v(-1, 1.88) * mm, "end": v(1, 1.88) * mm});
            skLineSegment(sketch, "E41.top", {"start": v(-1, 0.88) * mm, "end": v(1, 0.88) * mm});
            skLineSegment(sketch, "E41.left", {"start": v(-1, 1.88) * mm, "end": v(-1, 0.88) * mm});
            skLineSegment(sketch, "E41.right", {"start": v(1, 1.88) * mm, "end": v(1, 0.88) * mm});
            skLineSegment(sketch, "E42.bottom", {"start": v(32.5, 1.88) * mm, "end": v(34.5, 1.88) * mm});
            skLineSegment(sketch, "E42.top", {"start": v(32.5, 0.88) * mm, "end": v(34.5, 0.88) * mm});
            skLineSegment(sketch, "E42.left", {"start": v(32.5, 1.88) * mm, "end": v(32.5, 0.88) * mm});
            skLineSegment(sketch, "E42.right", {"start": v(34.5, 1.88) * mm, "end": v(34.5, 0.88) * mm});
            skLineSegment(sketch, "E43.bottom", {"start": v(67.5, 1.88) * mm, "end": v(69.5, 1.88) * mm});
            skLineSegment(sketch, "E43.top", {"start": v(67.5, 0.88) * mm, "end": v(69.5, 0.88) * mm});
            skLineSegment(sketch, "E43.left", {"start": v(67.5, 1.88) * mm, "end": v(67.5, 0.88) * mm});
            skLineSegment(sketch, "E43.right", {"start": v(69.5, 1.88) * mm, "end": v(69.5, 0.88) * mm});
            skSolve(sketch);
        }
        {
            var Q0;
            Q0 = qSketchRegion(id + "F28", true);
            extrude(context, id + "F29", {"entities" : qUnion([Q0]), "operationType" : NewBodyOperationType.ADD, "depth" : 0.7 * mm});
        }
        {
            var Q0;
            {var subQ4=makeQuery(id+"F3.opExtrude","SWEPT_FACE",FACE,{"disambiguationData":[OSD([sQuery(id+"F2.wireOp",EDGE,"E10.right")])]});var subQ5=makeQuery(id+"F3.opExtrude","SWEPT_FACE",FACE,{"disambiguationData":[OSD([sQuery(id+"F2.wireOp",EDGE,"E11.left")])]});var subQ6=sQuery(id+"F0.wireOp",EDGE,"E0");var subQ7=makeQuery(id+"F1.opExtrude","SWEPT_FACE",FACE,{"disambiguationData":[OSD([subQ6])]});var subQ8=makeQuery(id+"F3.boolean.opBoolean","SPLIT",FACE,{"disambiguationData":[TD([subQ4])],"derivedFrom":subQ7});Q0=makeQuery(id+"F7.boolean.opBoolean","MERGE",FACE,{"derivedFrom":[makeQuery(id+"F3.boolean.opBoolean","SPLIT",FACE,{"disambiguationData":[TD([makeQuery(id+"F3.opExtrude","SWEPT_FACE",FACE,{"disambiguationData":[OSD([sQuery(id+"F2.wireOp",EDGE,"E10.left")])]})])],"derivedFrom":subQ7}),makeQuery(id+"F3.boolean.opBoolean","SPLIT",FACE,{"disambiguationData":[TD([makeQuery(id+"F3.opExtrude","SWEPT_FACE",FACE,{"disambiguationData":[OSD([sQuery(id+"F2.wireOp",EDGE,"E11.right")])]})])],"derivedFrom":subQ7}),makeQuery(id+"F5.boolean.opBoolean","SPLIT",FACE,{"disambiguationData":[TD([makeQuery(id+"F3.boolean.opBoolean","COPY",FACE,{"derivedFrom":subQ4})])],"derivedFrom":subQ8}),makeQuery(id+"F5.boolean.opBoolean","SPLIT",FACE,{"disambiguationData":[TD([makeQuery(id+"F3.boolean.opBoolean","COPY",FACE,{"derivedFrom":subQ5})])],"derivedFrom":subQ8}),makeQuery(id+"F5.boolean.opBoolean","SPLIT",FACE,{"disambiguationData":[TD([makeQuery(id+"F5.opExtrude","SWEPT_FACE",FACE,{"disambiguationData":[OSD([sQuery(id+"F4.wireOp",EDGE,"E12.right")])]})])],"derivedFrom":subQ8}),makeQuery(id+"F7.opExtrude","SWEPT_FACE",FACE,{"disambiguationData":[OSD([sQuery(id+"F6.wireOp",EDGE,"E14.left")])]})]});}
            var sketch = newSketch(context, id + "F30", { "sketchPlane" : qUnion([Q0])});
            skLineSegment(sketch, "E44.bottom", {"start": v(-69.5, 1.88) * mm, "end": v(-67.5, 1.88) * mm});
            skLineSegment(sketch, "E44.top", {"start": v(-69.5, 0.88) * mm, "end": v(-67.5, 0.88) * mm});
            skLineSegment(sketch, "E44.left", {"start": v(-69.5, 1.88) * mm, "end": v(-69.5, 0.88) * mm});
            skLineSegment(sketch, "E44.right", {"start": v(-67.5, 1.88) * mm, "end": v(-67.5, 0.88) * mm});
            skLineSegment(sketch, "E45.bottom", {"start": v(-34.5, 1.88) * mm, "end": v(-32.5, 1.88) * mm});
            skLineSegment(sketch, "E45.top", {"start": v(-34.5, 0.88) * mm, "end": v(-32.5, 0.88) * mm});
            skLineSegment(sketch, "E45.left", {"start": v(-34.5, 1.88) * mm, "end": v(-34.5, 0.88) * mm});
            skLineSegment(sketch, "E45.right", {"start": v(-32.5, 1.88) * mm, "end": v(-32.5, 0.88) * mm});
            skLineSegment(sketch, "E46.bottom", {"start": v(-1, 1.88) * mm, "end": v(1, 1.88) * mm});
            skLineSegment(sketch, "E46.top", {"start": v(-1, 0.88) * mm, "end": v(1, 0.88) * mm});
            skLineSegment(sketch, "E46.left", {"start": v(-1, 1.88) * mm, "end": v(-1, 0.88) * mm});
            skLineSegment(sketch, "E46.right", {"start": v(1, 1.88) * mm, "end": v(1, 0.88) * mm});
            skLineSegment(sketch, "E47.bottom", {"start": v(32.5, 1.88) * mm, "end": v(34.5, 1.88) * mm});
            skLineSegment(sketch, "E47.top", {"start": v(32.5, 0.88) * mm, "end": v(34.5, 0.88) * mm});
            skLineSegment(sketch, "E47.left", {"start": v(32.5, 1.88) * mm, "end": v(32.5, 0.88) * mm});
            skLineSegment(sketch, "E47.right", {"start": v(34.5, 1.88) * mm, "end": v(34.5, 0.88) * mm});
            skLineSegment(sketch, "E48.bottom", {"start": v(67.5, 1.88) * mm, "end": v(69.5, 1.88) * mm});
            skLineSegment(sketch, "E48.top", {"start": v(67.5, 0.88) * mm, "end": v(69.5, 0.88) * mm});
            skLineSegment(sketch, "E48.left", {"start": v(67.5, 1.88) * mm, "end": v(67.5, 0.88) * mm});
            skLineSegment(sketch, "E48.right", {"start": v(69.5, 1.88) * mm, "end": v(69.5, 0.88) * mm});
            skSolve(sketch);
        }
        {
            var Q0;
            Q0 = qSketchRegion(id + "F30", true);
            extrude(context, id + "F31", {"entities" : qUnion([Q0]), "operationType" : NewBodyOperationType.ADD, "depth" : 0.7 * mm});
        }
        {
            var Q0;
            Q0=makeQuery(id+"F1.opExtrude","SWEPT_FACE",FACE,{"disambiguationData":[OSD([sQuery(id+"F0.wireOp",EDGE,"E5")])]});
            var sketch = newSketch(context, id + "F32", { "sketchPlane" : qUnion([Q0])});
            skLineSegment(sketch, "E49.bottom", {"start": v(67.5, 4) * mm, "end": v(69.5, 4) * mm});
            skLineSegment(sketch, "E49.top", {"start": v(67.5, -4) * mm, "end": v(69.5, -4) * mm});
            skLineSegment(sketch, "E49.left", {"start": v(67.5, 4) * mm, "end": v(67.5, -4) * mm});
            skLineSegment(sketch, "E49.right", {"start": v(69.5, 4) * mm, "end": v(69.5, -4) * mm});
            skLineSegment(sketch, "E50.bottom", {"start": v(32.5, 4) * mm, "end": v(34.5, 4) * mm});
            skLineSegment(sketch, "E50.top", {"start": v(32.5, -4) * mm, "end": v(34.5, -4) * mm});
            skLineSegment(sketch, "E50.left", {"start": v(32.5, 4) * mm, "end": v(32.5, -4) * mm});
            skLineSegment(sketch, "E50.right", {"start": v(34.5, 4) * mm, "end": v(34.5, -4) * mm});
            skLineSegment(sketch, "E51.bottom", {"start": v(-1, 4) * mm, "end": v(1, 4) * mm});
            skLineSegment(sketch, "E51.top", {"start": v(-1, -4) * mm, "end": v(1, -4) * mm});
            skLineSegment(sketch, "E51.left", {"start": v(-1, 4) * mm, "end": v(-1, -4) * mm});
            skLineSegment(sketch, "E51.right", {"start": v(1, 4) * mm, "end": v(1, -4) * mm});
            skLineSegment(sketch, "E52.bottom", {"start": v(-34.5, 4) * mm, "end": v(-32.5, 4) * mm});
            skLineSegment(sketch, "E52.top", {"start": v(-34.5, -4) * mm, "end": v(-32.5, -4) * mm});
            skLineSegment(sketch, "E52.left", {"start": v(-34.5, 4) * mm, "end": v(-34.5, -4) * mm});
            skLineSegment(sketch, "E52.right", {"start": v(-32.5, 4) * mm, "end": v(-32.5, -4) * mm});
            skLineSegment(sketch, "E53.bottom", {"start": v(-69.5, 4) * mm, "end": v(-67.5, 4) * mm});
            skLineSegment(sketch, "E53.top", {"start": v(-69.5, -4) * mm, "end": v(-67.5, -4) * mm});
            skLineSegment(sketch, "E53.left", {"start": v(-69.5, 4) * mm, "end": v(-69.5, -4) * mm});
            skLineSegment(sketch, "E53.right", {"start": v(-67.5, 4) * mm, "end": v(-67.5, -4) * mm});
            skSolve(sketch);
        }
        {
            var Q0;
            Q0 = qSketchRegion(id + "F32", true);
            extrude(context, id + "F33", {"entities" : qUnion([Q0]), "operationType" : NewBodyOperationType.ADD, "depth" : 0.25 * mm});
        }
        {
            var Q0;
            Q0=makeQuery(id+"F17.opExtrude","CAP_FACE",FACE,{"disambiguationData":[OSD([sQuery(id+"F16.wireOp",EDGE,"E25.bottom"),sQuery(id+"F16.wireOp",EDGE,"E25.top"),sQuery(id+"F16.wireOp",EDGE,"E25.left"),sQuery(id+"F16.wireOp",EDGE,"E25.right"),sQuery(id+"F16.wireOp",EDGE,"E26.filletArc"),sQuery(id+"F16.wireOp",EDGE,"E27.filletArc"),sQuery(id+"F16.wireOp",EDGE,"E28.filletArc"),sQuery(id+"F16.wireOp",EDGE,"E29.filletArc")])],"isStart":false});
            var sketch = newSketch(context, id + "F34", { "sketchPlane" : qUnion([Q0])});
            skCircle(sketch, "E54", {"center": v(49, 2.8) * mm, "radius": 0.35 * mm});
            skCircle(sketch, "E55", {"center": v(53, 2.8) * mm, "radius": 0.35 * mm});
            skCircle(sketch, "E56", {"center": v(49, -2.8) * mm, "radius": 0.35 * mm});
            skCircle(sketch, "E57", {"center": v(53, -2.8) * mm, "radius": 0.35 * mm});
            skSolve(sketch);
        }
        {
            var Q0;
            Q0 = qSketchRegion(id + "F34", true);
            extrude(context, id + "F35", {"entities" : qUnion([Q0]), "operationType" : NewBodyOperationType.ADD, "depth" : 0.5 * mm});
        }
        {
            var Q0;
            Q0=makeQuery(id+"F17.opExtrude","CAP_FACE",FACE,{"disambiguationData":[OSD([sQuery(id+"F16.wireOp",EDGE,"E24.bottom"),sQuery(id+"F16.wireOp",EDGE,"E24.top"),sQuery(id+"F16.wireOp",EDGE,"E24.left"),sQuery(id+"F16.wireOp",EDGE,"E24.right"),sQuery(id+"F16.wireOp",EDGE,"E30.filletArc"),sQuery(id+"F16.wireOp",EDGE,"E31.filletArc"),sQuery(id+"F16.wireOp",EDGE,"E32.filletArc"),sQuery(id+"F16.wireOp",EDGE,"E33.filletArc")])],"isStart":false});
            var sketch = newSketch(context, id + "F36", { "sketchPlane" : qUnion([Q0])});
            skCircle(sketch, "E58", {"center": v(-53, 2.8) * mm, "radius": 0.35 * mm});
            skCircle(sketch, "E59", {"center": v(-49, 2.8) * mm, "radius": 0.35 * mm});
            skCircle(sketch, "E60", {"center": v(-49, -2.8) * mm, "radius": 0.35 * mm});
            skCircle(sketch, "E61", {"center": v(-53, -2.8) * mm, "radius": 0.35 * mm});
            skSolve(sketch);
        }
        {
            var Q0;
            Q0 = qSketchRegion(id + "F36", true);
            extrude(context, id + "F37", {"entities" : qUnion([Q0]), "operationType" : NewBodyOperationType.ADD, "depth" : 0.5 * mm});
        }
        {
            var Q0;
            Q0=makeQuery(id+"F33.opExtrude","SWEPT_EDGE",EDGE,{"disambiguationData":[OSD([sQuery(id+"F32.wireOp",EDGE,"E49.bottom"),sQuery(id+"F32.wireOp",EDGE,"E49.right")])]});
            var Q1;
            Q1=makeQuery(id+"F33.opExtrude","SWEPT_EDGE",EDGE,{"disambiguationData":[OSD([sQuery(id+"F32.wireOp",EDGE,"E49.top"),sQuery(id+"F32.wireOp",EDGE,"E49.right")])]});
            var Q2;
            Q2=makeQuery(id+"F33.opExtrude","SWEPT_EDGE",EDGE,{"disambiguationData":[OSD([sQuery(id+"F32.wireOp",EDGE,"E49.bottom"),sQuery(id+"F32.wireOp",EDGE,"E49.left")])]});
            var Q3;
            Q3=makeQuery(id+"F33.opExtrude","SWEPT_EDGE",EDGE,{"disambiguationData":[OSD([sQuery(id+"F32.wireOp",EDGE,"E49.top"),sQuery(id+"F32.wireOp",EDGE,"E49.left")])]});
            var Q4;
            Q4=makeQuery(id+"F33.opExtrude","SWEPT_EDGE",EDGE,{"disambiguationData":[OSD([sQuery(id+"F32.wireOp",EDGE,"E50.bottom"),sQuery(id+"F32.wireOp",EDGE,"E50.left")])]});
            var Q5;
            Q5=makeQuery(id+"F33.opExtrude","SWEPT_EDGE",EDGE,{"disambiguationData":[OSD([sQuery(id+"F32.wireOp",EDGE,"E50.top"),sQuery(id+"F32.wireOp",EDGE,"E50.left")])]});
            var Q6;
            Q6=makeQuery(id+"F33.opExtrude","SWEPT_EDGE",EDGE,{"disambiguationData":[OSD([sQuery(id+"F32.wireOp",EDGE,"E50.top"),sQuery(id+"F32.wireOp",EDGE,"E50.right")])]});
            var Q7;
            Q7=makeQuery(id+"F33.opExtrude","SWEPT_EDGE",EDGE,{"disambiguationData":[OSD([sQuery(id+"F32.wireOp",EDGE,"E50.bottom"),sQuery(id+"F32.wireOp",EDGE,"E50.right")])]});
            var Q8;
            Q8=makeQuery(id+"F33.opExtrude","SWEPT_EDGE",EDGE,{"disambiguationData":[OSD([sQuery(id+"F32.wireOp",EDGE,"E51.bottom"),sQuery(id+"F32.wireOp",EDGE,"E51.right")])]});
            var Q9;
            Q9=makeQuery(id+"F33.opExtrude","SWEPT_EDGE",EDGE,{"disambiguationData":[OSD([sQuery(id+"F32.wireOp",EDGE,"E51.top"),sQuery(id+"F32.wireOp",EDGE,"E51.right")])]});
            var Q10;
            Q10=makeQuery(id+"F33.opExtrude","SWEPT_EDGE",EDGE,{"disambiguationData":[OSD([sQuery(id+"F32.wireOp",EDGE,"E51.top"),sQuery(id+"F32.wireOp",EDGE,"E51.left")])]});
            var Q11;
            Q11=makeQuery(id+"F33.opExtrude","SWEPT_EDGE",EDGE,{"disambiguationData":[OSD([sQuery(id+"F32.wireOp",EDGE,"E51.bottom"),sQuery(id+"F32.wireOp",EDGE,"E51.left")])]});
            var Q12;
            Q12=makeQuery(id+"F33.opExtrude","SWEPT_EDGE",EDGE,{"disambiguationData":[OSD([sQuery(id+"F32.wireOp",EDGE,"E52.bottom"),sQuery(id+"F32.wireOp",EDGE,"E52.left")])]});
            var Q13;
            Q13=makeQuery(id+"F33.opExtrude","SWEPT_EDGE",EDGE,{"disambiguationData":[OSD([sQuery(id+"F32.wireOp",EDGE,"E52.top"),sQuery(id+"F32.wireOp",EDGE,"E52.left")])]});
            var Q14;
            Q14=makeQuery(id+"F33.opExtrude","SWEPT_EDGE",EDGE,{"disambiguationData":[OSD([sQuery(id+"F32.wireOp",EDGE,"E52.bottom"),sQuery(id+"F32.wireOp",EDGE,"E52.right")])]});
            var Q15;
            Q15=makeQuery(id+"F33.opExtrude","SWEPT_EDGE",EDGE,{"disambiguationData":[OSD([sQuery(id+"F32.wireOp",EDGE,"E52.top"),sQuery(id+"F32.wireOp",EDGE,"E52.right")])]});
            var Q16;
            Q16=makeQuery(id+"F33.opExtrude","SWEPT_EDGE",EDGE,{"disambiguationData":[OSD([sQuery(id+"F32.wireOp",EDGE,"E53.bottom"),sQuery(id+"F32.wireOp",EDGE,"E53.right")])]});
            var Q17;
            Q17=makeQuery(id+"F33.opExtrude","SWEPT_EDGE",EDGE,{"disambiguationData":[OSD([sQuery(id+"F32.wireOp",EDGE,"E53.top"),sQuery(id+"F32.wireOp",EDGE,"E53.right")])]});
            var Q18;
            Q18=makeQuery(id+"F33.opExtrude","SWEPT_EDGE",EDGE,{"disambiguationData":[OSD([sQuery(id+"F32.wireOp",EDGE,"E53.bottom"),sQuery(id+"F32.wireOp",EDGE,"E53.left")])]});
            var Q19;
            Q19=makeQuery(id+"F33.opExtrude","SWEPT_EDGE",EDGE,{"disambiguationData":[OSD([sQuery(id+"F32.wireOp",EDGE,"E53.top"),sQuery(id+"F32.wireOp",EDGE,"E53.left")])]});
            fillet(context, id + "F38", {"entities" : qUnion([Q0, Q1, Q2, Q3, Q4, Q5, Q6, Q7, Q8, Q9, Q10, Q11, Q12, Q13, Q14, Q15, Q16, Q17, Q18, Q19]), "radius" : 0.5 * mm, "tangentPropagation" : true, "allowEdgeOverflow" : false});
        }
        {
            var Q0;
            Q0=makeQuery(id+"F33.opExtrude","CAP_FACE",FACE,{"disambiguationData":[OSD([sQuery(id+"F32.wireOp",EDGE,"E49.bottom"),sQuery(id+"F32.wireOp",EDGE,"E49.top"),sQuery(id+"F32.wireOp",EDGE,"E49.left"),sQuery(id+"F32.wireOp",EDGE,"E49.right")])],"isStart":false});
            var sketch = newSketch(context, id + "F39", { "sketchPlane" : qUnion([Q0])});
            skCircle(sketch, "E62", {"center": v(68.5, 3) * mm, "radius": 0.25 * mm});
            skCircle(sketch, "E63", {"center": v(68.5, -3) * mm, "radius": 0.25 * mm});
            skCircle(sketch, "E64", {"center": v(33.5, 3) * mm, "radius": 0.25 * mm});
            skCircle(sketch, "E65", {"center": v(33.5, -3) * mm, "radius": 0.25 * mm});
            skCircle(sketch, "E66", {"center": v(0, 3) * mm, "radius": 0.25 * mm});
            skCircle(sketch, "E67", {"center": v(0, -3) * mm, "radius": 0.25 * mm});
            skCircle(sketch, "E68", {"center": v(-33.5, 3) * mm, "radius": 0.25 * mm});
            skCircle(sketch, "E69", {"center": v(-33.5, -3) * mm, "radius": 0.25 * mm});
            skCircle(sketch, "E70", {"center": v(-68.5, 3) * mm, "radius": 0.25 * mm});
            skCircle(sketch, "E71", {"center": v(-68.5, -3) * mm, "radius": 0.25 * mm});
            skSolve(sketch);
        }
        {
            var Q0;
            Q0 = qSketchRegion(id + "F39", true);
            extrude(context, id + "F40", {"entities" : qUnion([Q0]), "operationType" : NewBodyOperationType.ADD, "depth" : 0.5 * mm});
        }
        {
            var Q0;
            {var subQ4=makeQuery(id+"F3.opExtrude","SWEPT_FACE",FACE,{"disambiguationData":[OSD([sQuery(id+"F2.wireOp",EDGE,"E10.right")])]});var subQ5=makeQuery(id+"F3.opExtrude","SWEPT_FACE",FACE,{"disambiguationData":[OSD([sQuery(id+"F2.wireOp",EDGE,"E11.left")])]});var subQ6=sQuery(id+"F0.wireOp",EDGE,"E1");var subQ7=makeQuery(id+"F1.opExtrude","SWEPT_FACE",FACE,{"disambiguationData":[OSD([subQ6])]});var subQ8=makeQuery(id+"F3.boolean.opBoolean","SPLIT",FACE,{"disambiguationData":[TD([subQ4])],"derivedFrom":subQ7});Q0=makeQuery(id+"F27.boolean.opBoolean","MERGE",FACE,{"derivedFrom":[makeQuery(id+"F11.boolean.opBoolean","MERGE",FACE,{"derivedFrom":[makeQuery(id+"F7.boolean.opBoolean","MERGE",FACE,{"derivedFrom":[makeQuery(id+"F3.boolean.opBoolean","SPLIT",FACE,{"disambiguationData":[TD([makeQuery(id+"F3.opExtrude","SWEPT_FACE",FACE,{"disambiguationData":[OSD([sQuery(id+"F2.wireOp",EDGE,"E10.left")])]})])],"derivedFrom":subQ7}),makeQuery(id+"F3.boolean.opBoolean","SPLIT",FACE,{"disambiguationData":[TD([makeQuery(id+"F3.opExtrude","SWEPT_FACE",FACE,{"disambiguationData":[OSD([sQuery(id+"F2.wireOp",EDGE,"E11.right")])]})])],"derivedFrom":subQ7}),makeQuery(id+"F5.boolean.opBoolean","SPLIT",FACE,{"disambiguationData":[TD([makeQuery(id+"F3.boolean.opBoolean","COPY",FACE,{"derivedFrom":subQ4})])],"derivedFrom":subQ8}),makeQuery(id+"F5.boolean.opBoolean","SPLIT",FACE,{"disambiguationData":[TD([makeQuery(id+"F3.boolean.opBoolean","COPY",FACE,{"derivedFrom":subQ5})])],"derivedFrom":subQ8}),makeQuery(id+"F5.boolean.opBoolean","SPLIT",FACE,{"disambiguationData":[TD([makeQuery(id+"F5.opExtrude","SWEPT_FACE",FACE,{"disambiguationData":[OSD([sQuery(id+"F4.wireOp",EDGE,"E12.right")])]})])],"derivedFrom":subQ8}),makeQuery(id+"F7.opExtrude","SWEPT_FACE",FACE,{"disambiguationData":[OSD([sQuery(id+"F6.wireOp",EDGE,"E14.top")])]}),makeQuery(id+"F7.opExtrude","SWEPT_FACE",FACE,{"disambiguationData":[OSD([sQuery(id+"F6.wireOp",EDGE,"E15.top")])]})]}),makeQuery(id+"F11.opExtrude","SWEPT_FACE",FACE,{"disambiguationData":[OSD([sQuery(id+"F10.wireOp",EDGE,"E18.bottom")])]}),makeQuery(id+"F11.opExtrude","SWEPT_FACE",FACE,{"disambiguationData":[OSD([sQuery(id+"F10.wireOp",EDGE,"E19.top")])]})]}),makeQuery(id+"F27.opExtrude","CAP_FACE",FACE,{"disambiguationData":[OSD([sQuery(id+"F26.wireOp",EDGE,"E38.bottom"),sQuery(id+"F26.wireOp",EDGE,"E38.top"),sQuery(id+"F26.wireOp",EDGE,"E38.left"),sQuery(id+"F26.wireOp",EDGE,"E38.right")])],"isStart":true})]});}
            var sketch = newSketch(context, id + "F41", { "sketchPlane" : qUnion([Q0])});
            skLineSegment(sketch, "E72.bottom", {"start": v(-35, 0) * mm, "end": v(35, 0) * mm});
            skLineSegment(sketch, "E72.top", {"start": v(-35, -1) * mm, "end": v(35, -1) * mm});
            skLineSegment(sketch, "E72.left", {"start": v(-35, 0) * mm, "end": v(-35, -1) * mm});
            skLineSegment(sketch, "E72.right", {"start": v(35, 0) * mm, "end": v(35, -1) * mm});
            skSolve(sketch);
        }
        {
            var Q0;
            Q0=makeQuery(id+"F41.imprint","IMPRINT",FACE,{"disambiguationData":[TD([[makeQuery(id+"F41.imprint","IMPRINT",EDGE,{"derivedFrom":sQuery(id+"F41.wireOp",EDGE,"E72.bottom")}),-1.0]])]});
            extrude(context, id + "F42", {"entities" : qUnion([Q0]), "operationType" : NewBodyOperationType.ADD, "oppositeDirection" : true, "depth" : 9 * mm});
        }
        {
            var Q0;
            Q0=qCreatedBy(makeId("Front.planeOp"),FACE);
            var sketch = newSketch(context, id + "F43", { "sketchPlane" : qUnion([Q0])});
            skCircle(sketch, "E73", {"center": v(-50.93, 0.75) * mm, "radius": 0.43 * mm});
            skCircle(sketch, "E74", {"center": v(50.99, 0.76) * mm, "radius": 0.42 * mm});
            skSolve(sketch);
        }
        {
            var Q0;
            Q0 = qSketchRegion(id + "F43", true);
            extrude(context, id + "F44", {"entities" : qUnion([Q0]), "operationType" : NewBodyOperationType.REMOVE, "endBound" : BoundingType.SYMMETRIC, "oppositeDirection" : true, "depth" : 5 * mm});
        }
        {
            var Q0;
            Q0=makeQuery(id+"F21.boolean.opBoolean","MERGE",FACE,{"derivedFrom":[makeQuery(id+"F3.boolean.opBoolean","COPY",FACE,{"derivedFrom":makeQuery(id+"F3.opExtrude","SWEPT_FACE",FACE,{"disambiguationData":[OSD([sQuery(id+"F2.wireOp",EDGE,"E11.bottom")])]})}),makeQuery(id+"F21.opExtrude","SWEPT_FACE",FACE,{"disambiguationData":[OSD([sQuery(id+"F20.wireOp",EDGE,"E35.bottom")])]})]});
            var sketch = newSketch(context, id + "F45", { "sketchPlane" : qUnion([Q0])});
            skLineSegment(sketch, "E75.bottom", {"start": v(35, 1) * mm, "end": v(45, 1) * mm});
            skLineSegment(sketch, "E75.top", {"start": v(35, -1) * mm, "end": v(45, -1) * mm});
            skLineSegment(sketch, "E75.left", {"start": v(35, 1) * mm, "end": v(35, -1) * mm});
            skLineSegment(sketch, "E75.right", {"start": v(45, 1) * mm, "end": v(45, -1) * mm});
            skLineSegment(sketch, "E76.bottom", {"start": v(-35, 1) * mm, "end": v(-45, 1) * mm});
            skLineSegment(sketch, "E76.top", {"start": v(-35, -1) * mm, "end": v(-45, -1) * mm});
            skLineSegment(sketch, "E76.left", {"start": v(-35, 1) * mm, "end": v(-35, -1) * mm});
            skLineSegment(sketch, "E76.right", {"start": v(-45, 1) * mm, "end": v(-45, -1) * mm});
            skSolve(sketch);
        }
        {
            var Q0;
            Q0 = qSketchRegion(id + "F45", true);
            extrude(context, id + "F46", {"entities" : qUnion([Q0]), "operationType" : NewBodyOperationType.ADD, "depth" : 3 * mm});
        }
        {
            var Q0;
            Q0=makeQuery(id+"F46.opExtrude","SWEPT_FACE",FACE,{"disambiguationData":[OSD([sQuery(id+"F45.wireOp",EDGE,"E75.bottom")])]});
            var sketch = newSketch(context, id + "F47", { "sketchPlane" : qUnion([Q0])});
            skLineSegment(sketch, "E77", {"start": v(45, 7.38) * mm, "end": v(45, 4.38) * mm});
            skLineSegment(sketch, "E78", {"start": v(45, 4.38) * mm, "end": v(42, 4.38) * mm});
            skLineSegment(sketch, "E79", {"start": v(42, 4.38) * mm, "end": v(45, 7.38) * mm});
            skLineSegment(sketch, "E80", {"start": v(-45.03, 4.36) * mm, "end": v(-42.03, 4.36) * mm});
            skLineSegment(sketch, "E81", {"start": v(-42.03, 4.36) * mm, "end": v(-45.04, 7.36) * mm});
            skLineSegment(sketch, "E82", {"start": v(-45.04, 7.36) * mm, "end": v(-45.03, 4.36) * mm});
            skSolve(sketch);
        }
        {
            var Q0;
            Q0 = qSketchRegion(id + "F47", true);
            extrude(context, id + "F48", {"entities" : qUnion([Q0]), "operationType" : NewBodyOperationType.REMOVE, "oppositeDirection" : true, "depth" : 2 * mm});
        }
        {
            var Q0;
            Q0=makeQuery(id+"F25.boolean.opBoolean","MERGE",FACE,{"derivedFrom":[makeQuery(id+"F3.boolean.opBoolean","COPY",FACE,{"derivedFrom":makeQuery(id+"F3.opExtrude","SWEPT_FACE",FACE,{"disambiguationData":[OSD([sQuery(id+"F2.wireOp",EDGE,"E10.bottom")])]})}),makeQuery(id+"F25.opExtrude","SWEPT_FACE",FACE,{"disambiguationData":[OSD([sQuery(id+"F24.wireOp",EDGE,"E37.bottom")])]})]});
            var sketch = newSketch(context, id + "F49", { "sketchPlane" : qUnion([Q0])});
            skLineSegment(sketch, "E83.bottom", {"start": v(-53.5, -11) * mm, "end": v(-48.5, -11) * mm});
            skLineSegment(sketch, "E83.top", {"start": v(-53.5, 11) * mm, "end": v(-48.5, 11) * mm});
            skLineSegment(sketch, "E83.left", {"start": v(-53.5, -11) * mm, "end": v(-53.5, 11) * mm});
            skLineSegment(sketch, "E83.right", {"start": v(-48.5, -11) * mm, "end": v(-48.5, 11) * mm});
            skLineSegment(sketch, "E84.bottom", {"start": v(48.53, 11) * mm, "end": v(53.53, 11) * mm});
            skLineSegment(sketch, "E84.top", {"start": v(48.53, -11) * mm, "end": v(53.53, -11) * mm});
            skLineSegment(sketch, "E84.left", {"start": v(48.53, 11) * mm, "end": v(48.53, -11) * mm});
            skLineSegment(sketch, "E84.right", {"start": v(53.53, 11) * mm, "end": v(53.53, -11) * mm});
            skSolve(sketch);
        }
        {
            var Q0;
            Q0=makeQuery(id+"F49.imprint","IMPRINT",FACE,{"disambiguationData":[TD([[makeQuery(id+"F49.imprint","IMPRINT",EDGE,{"derivedFrom":sQuery(id+"F49.wireOp",EDGE,"E84.bottom")}),-1.0]])]});
            extrude(context, id + "F50", {"entities" : qUnion([Q0]), "operationType" : NewBodyOperationType.ADD, "oppositeDirection" : true, "depth" : 1 * mm});
        }
        {
            var Q0;
            Q0=makeQuery(id+"F50.boolean.opBoolean","MERGE",FACE,{"derivedFrom":[makeQuery(id+"F1.opExtrude","SWEPT_FACE",FACE,{"disambiguationData":[OSD([sQuery(id+"F0.wireOp",EDGE,"E5")])]}),makeQuery(id+"F50.opExtrude","CAP_FACE",FACE,{"disambiguationData":[OSD([sQuery(id+"F49.wireOp",EDGE,"E84.bottom"),sQuery(id+"F49.wireOp",EDGE,"E84.top"),sQuery(id+"F49.wireOp",EDGE,"E84.left"),sQuery(id+"F49.wireOp",EDGE,"E84.right")])],"isStart":false})]});
            var sketch = newSketch(context, id + "F51", { "sketchPlane" : qUnion([Q0])});
            skLineSegment(sketch, "E85.bottom", {"start": v(-53.5, 11) * mm, "end": v(-48.5, 11) * mm});
            skLineSegment(sketch, "E85.top", {"start": v(-53.5, -11) * mm, "end": v(-48.5, -11) * mm});
            skLineSegment(sketch, "E85.left", {"start": v(-53.5, 11) * mm, "end": v(-53.5, -11) * mm});
            skLineSegment(sketch, "E85.right", {"start": v(-48.5, 11) * mm, "end": v(-48.5, -11) * mm});
            skSolve(sketch);
        }
        {
            var Q0;
            Q0 = qSketchRegion(id + "F51", true);
            extrude(context, id + "F52", {"entities" : qUnion([Q0]), "operationType" : NewBodyOperationType.ADD, "oppositeDirection" : true, "depth" : 1 * mm});
        }
        {
            var Q0;
            Q0=makeQuery(id+"F52.opExtrude","SWEPT_EDGE",EDGE,{"disambiguationData":[OSD([sQuery(id+"F51.wireOp",EDGE,"E85.top"),sQuery(id+"F51.wireOp",EDGE,"E85.left")])]});
            var Q1;
            Q1=makeQuery(id+"F52.opExtrude","SWEPT_EDGE",EDGE,{"disambiguationData":[OSD([sQuery(id+"F51.wireOp",EDGE,"E85.top"),sQuery(id+"F51.wireOp",EDGE,"E85.right")])]});
            var Q2;
            Q2=makeQuery(id+"F52.opExtrude","SWEPT_EDGE",EDGE,{"disambiguationData":[OSD([sQuery(id+"F51.wireOp",EDGE,"E85.bottom"),sQuery(id+"F51.wireOp",EDGE,"E85.left")])]});
            var Q3;
            Q3=makeQuery(id+"F52.opExtrude","SWEPT_EDGE",EDGE,{"disambiguationData":[OSD([sQuery(id+"F51.wireOp",EDGE,"E85.bottom"),sQuery(id+"F51.wireOp",EDGE,"E85.right")])]});
            var Q4;
            Q4=makeQuery(id+"F50.opExtrude","SWEPT_EDGE",EDGE,{"disambiguationData":[OSD([sQuery(id+"F49.wireOp",EDGE,"E84.top"),sQuery(id+"F49.wireOp",EDGE,"E84.right")])]});
            var Q5;
            Q5=makeQuery(id+"F50.opExtrude","SWEPT_EDGE",EDGE,{"disambiguationData":[OSD([sQuery(id+"F49.wireOp",EDGE,"E84.top"),sQuery(id+"F49.wireOp",EDGE,"E84.left")])]});
            var Q6;
            Q6=makeQuery(id+"F50.opExtrude","SWEPT_EDGE",EDGE,{"disambiguationData":[OSD([sQuery(id+"F49.wireOp",EDGE,"E84.bottom"),sQuery(id+"F49.wireOp",EDGE,"E84.left")])]});
            var Q7;
            Q7=makeQuery(id+"F50.opExtrude","SWEPT_EDGE",EDGE,{"disambiguationData":[OSD([sQuery(id+"F49.wireOp",EDGE,"E84.bottom"),sQuery(id+"F49.wireOp",EDGE,"E84.right")])]});
            fillet(context, id + "F53", {"entities" : qUnion([Q0, Q1, Q2, Q3, Q4, Q5, Q6, Q7]), "radius" : 1 * mm, "tangentPropagation" : true, "allowEdgeOverflow" : false});
        }
        {
            var Q0;
            Q0=makeQuery(id+"F52.boolean.opBoolean","MERGE",FACE,{"derivedFrom":[makeQuery(id+"F50.boolean.opBoolean","MERGE",FACE,{"derivedFrom":[makeQuery(id+"F1.opExtrude","SWEPT_FACE",FACE,{"disambiguationData":[OSD([sQuery(id+"F0.wireOp",EDGE,"E5")])]}),makeQuery(id+"F50.opExtrude","CAP_FACE",FACE,{"disambiguationData":[OSD([sQuery(id+"F49.wireOp",EDGE,"E84.bottom"),sQuery(id+"F49.wireOp",EDGE,"E84.top"),sQuery(id+"F49.wireOp",EDGE,"E84.left"),sQuery(id+"F49.wireOp",EDGE,"E84.right")])],"isStart":false})]}),makeQuery(id+"F52.opExtrude","CAP_FACE",FACE,{"disambiguationData":[OSD([sQuery(id+"F51.wireOp",EDGE,"E85.bottom"),sQuery(id+"F51.wireOp",EDGE,"E85.top"),sQuery(id+"F51.wireOp",EDGE,"E85.left"),sQuery(id+"F51.wireOp",EDGE,"E85.right")])],"isStart":true})]});
            var sketch = newSketch(context, id + "F54", { "sketchPlane" : qUnion([Q0])});
            skLineSegment(sketch, "E86.bottom", {"start": v(49.53, 10) * mm, "end": v(52.53, 10) * mm});
            skLineSegment(sketch, "E86.top", {"start": v(49.53, -10) * mm, "end": v(52.53, -10) * mm});
            skLineSegment(sketch, "E86.left", {"start": v(49.53, 10) * mm, "end": v(49.53, -10) * mm});
            skLineSegment(sketch, "E86.right", {"start": v(52.53, 10) * mm, "end": v(52.53, -10) * mm});
            skLineSegment(sketch, "E87.bottom", {"start": v(-52.5, 10) * mm, "end": v(-49.5, 10) * mm});
            skLineSegment(sketch, "E87.top", {"start": v(-52.5, -10) * mm, "end": v(-49.5, -10) * mm});
            skLineSegment(sketch, "E87.left", {"start": v(-52.5, 10) * mm, "end": v(-52.5, -10) * mm});
            skLineSegment(sketch, "E87.right", {"start": v(-49.5, 10) * mm, "end": v(-49.5, -10) * mm});
            skSolve(sketch);
        }
        {
            var Q0;
            Q0 = qSketchRegion(id + "F54", true);
            extrude(context, id + "F55", {"entities" : qUnion([Q0]), "operationType" : NewBodyOperationType.ADD, "depth" : 0.3 * mm});
        }
        {
            var Q0;
            Q0=makeQuery(id+"F55.opExtrude","SWEPT_EDGE",EDGE,{"disambiguationData":[OSD([sQuery(id+"F54.wireOp",EDGE,"E86.top"),sQuery(id+"F54.wireOp",EDGE,"E86.right")])]});
            var Q1;
            Q1=makeQuery(id+"F55.opExtrude","SWEPT_EDGE",EDGE,{"disambiguationData":[OSD([sQuery(id+"F54.wireOp",EDGE,"E86.top"),sQuery(id+"F54.wireOp",EDGE,"E86.left")])]});
            var Q2;
            Q2=makeQuery(id+"F55.opExtrude","SWEPT_EDGE",EDGE,{"disambiguationData":[OSD([sQuery(id+"F54.wireOp",EDGE,"E86.bottom"),sQuery(id+"F54.wireOp",EDGE,"E86.right")])]});
            var Q3;
            Q3=makeQuery(id+"F55.opExtrude","SWEPT_EDGE",EDGE,{"disambiguationData":[OSD([sQuery(id+"F54.wireOp",EDGE,"E86.bottom"),sQuery(id+"F54.wireOp",EDGE,"E86.left")])]});
            var Q4;
            Q4=makeQuery(id+"F55.opExtrude","SWEPT_EDGE",EDGE,{"disambiguationData":[OSD([sQuery(id+"F54.wireOp",EDGE,"E87.bottom"),sQuery(id+"F54.wireOp",EDGE,"E87.left")])]});
            var Q5;
            Q5=makeQuery(id+"F55.opExtrude","SWEPT_EDGE",EDGE,{"disambiguationData":[OSD([sQuery(id+"F54.wireOp",EDGE,"E87.bottom"),sQuery(id+"F54.wireOp",EDGE,"E87.right")])]});
            var Q6;
            Q6=makeQuery(id+"F55.opExtrude","SWEPT_EDGE",EDGE,{"disambiguationData":[OSD([sQuery(id+"F54.wireOp",EDGE,"E87.top"),sQuery(id+"F54.wireOp",EDGE,"E87.left")])]});
            var Q7;
            Q7=makeQuery(id+"F55.opExtrude","SWEPT_EDGE",EDGE,{"disambiguationData":[OSD([sQuery(id+"F54.wireOp",EDGE,"E87.top"),sQuery(id+"F54.wireOp",EDGE,"E87.right")])]});
            fillet(context, id + "F56", {"entities" : qUnion([Q0, Q1, Q2, Q3, Q4, Q5, Q6, Q7]), "radius" : 1 * mm, "tangentPropagation" : true, "allowEdgeOverflow" : false});
        }
        {
            var Q0;
            {var subQ0=sQuery(id+"F54.wireOp",EDGE,"E86.top");var subQ1=sQuery(id+"F54.wireOp",EDGE,"E86.left");var subQ2=sQuery(id+"F54.wireOp",EDGE,"E86.right");Q0=makeQuery(id+"F55.boolean.opBoolean","SPLIT",FACE,{"disambiguationData":[TD([makeQuery(id+"F17.opExtrude","SWEPT_FACE",FACE,{"disambiguationData":[OSD([sQuery(id+"F16.wireOp",EDGE,"E25.top")])]})])],"derivedFrom":makeQuery(id+"F55.opExtrude","CAP_FACE",FACE,{"disambiguationData":[OSD([sQuery(id+"F54.wireOp",EDGE,"E86.bottom"),subQ0,subQ1,subQ2])],"isStart":false})});}
            var sketch = newSketch(context, id + "F57", { "sketchPlane" : qUnion([Q0])});
            skCircle(sketch, "E88", {"center": v(51.03, -9) * mm, "radius": 0.35 * mm});
            skCircle(sketch, "E89", {"center": v(51.03, 9) * mm, "radius": 0.35 * mm});
            skCircle(sketch, "E90", {"center": v(-51, 9) * mm, "radius": 0.35 * mm});
            skCircle(sketch, "E91", {"center": v(-51, -9) * mm, "radius": 0.35 * mm});
            skSolve(sketch);
        }
        {
            var Q0;
            Q0 = qSketchRegion(id + "F57", true);
            extrude(context, id + "F58", {"entities" : qUnion([Q0]), "operationType" : NewBodyOperationType.ADD, "depth" : 0.5 * mm});
        }
    });
